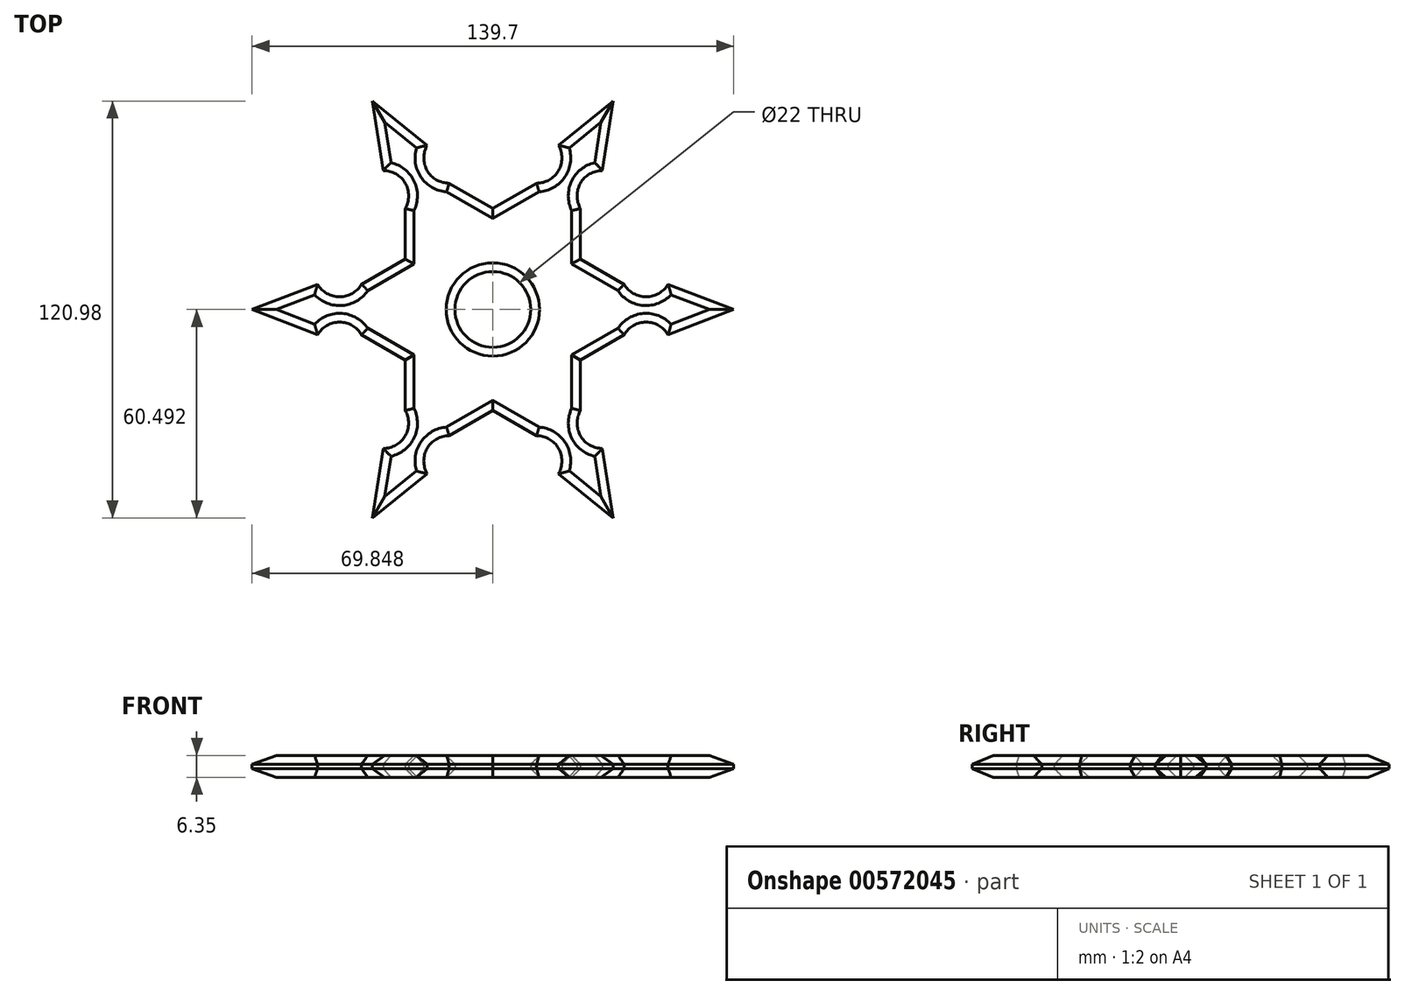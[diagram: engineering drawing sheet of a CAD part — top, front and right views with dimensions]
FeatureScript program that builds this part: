
annotation { "Feature Type Name" : "Feature", "Feature Type Description" : "" }
export const myFeature = defineFeature(function(context is Context, id is Id, definition is map)
    precondition{}
    {
        {
            var Q0;
            Q0=qCreatedBy(makeId("Top.planeOp"),FACE);
            var sketch = newSketch(context, id + "F0", { "sketchPlane" : qUnion([Q0])});
            skCircle(sketch, "E0.cCircle", {"center": v(-16.34, 15.72) * mm, "radius": 25.4 * mm, "construction": true});
            skLineSegment(sketch, "E0.0", {"start": v(9.06, 30.39) * mm, "end": v(9.06, 1.06) * mm});
            skLineSegment(sketch, "E0.1", {"start": v(9.06, 1.06) * mm, "end": v(-16.34, -13.6) * mm});
            skLineSegment(sketch, "E0.2", {"start": v(-16.34, -13.6) * mm, "end": v(-41.74, 1.06) * mm});
            skLineSegment(sketch, "E0.3", {"start": v(-41.74, 1.06) * mm, "end": v(-41.74, 30.39) * mm});
            skLineSegment(sketch, "E0.4", {"start": v(-41.74, 30.39) * mm, "end": v(-16.34, 45.05) * mm});
            skLineSegment(sketch, "E0.5", {"start": v(-16.34, 45.05) * mm, "end": v(9.06, 30.39) * mm});
            skPoint(sketch, "E0.0.midPoint", {"position": v(9.06, 15.72) * mm});
            skLineSegment(sketch, "E1", {"start": v(-16.34, 45.05) * mm, "end": v(-3.64, 52.38) * mm});
            skLineSegment(sketch, "E2", {"start": v(9.06, 30.39) * mm, "end": v(9.06, 45.05) * mm});
            skLineSegment(sketch, "E3", {"start": v(-3.64, 52.38) * mm, "end": v(9.06, 45.05) * mm});
            skLineSegment(sketch, "E4", {"start": v(-41.74, 30.39) * mm, "end": v(-41.74, 45.05) * mm});
            skLineSegment(sketch, "E5", {"start": v(-16.34, 45.05) * mm, "end": v(-29.04, 52.38) * mm});
            skLineSegment(sketch, "E6", {"start": v(-29.04, 52.38) * mm, "end": v(-41.74, 45.05) * mm});
            skLineSegment(sketch, "E7", {"start": v(-41.74, 30.39) * mm, "end": v(-54.44, 23.05) * mm});
            skLineSegment(sketch, "E8", {"start": v(-41.74, 1.06) * mm, "end": v(-54.44, 8.39) * mm});
            skLineSegment(sketch, "E9", {"start": v(-54.44, 23.05) * mm, "end": v(-54.44, 8.39) * mm});
            skLineSegment(sketch, "E10", {"start": v(-41.74, 1.06) * mm, "end": v(-41.74, -13.6) * mm});
            skPoint(sketch, "E11.endSnap0", {"position": v(-29.04, -6.28) * mm});
            skLineSegment(sketch, "E12", {"start": v(-16.34, -13.6) * mm, "end": v(-29.04, -20.94) * mm});
            skLineSegment(sketch, "E13", {"start": v(-41.74, -13.6) * mm, "end": v(-29.04, -20.94) * mm});
            skLineSegment(sketch, "E14", {"start": v(-16.34, -13.6) * mm, "end": v(-3.64, -20.94) * mm});
            skLineSegment(sketch, "E15", {"start": v(9.06, 1.06) * mm, "end": v(9.06, -13.6) * mm});
            skLineSegment(sketch, "E16", {"start": v(-3.64, -20.94) * mm, "end": v(9.06, -13.6) * mm});
            skLineSegment(sketch, "E17", {"start": v(9.06, 30.39) * mm, "end": v(21.76, 23.05) * mm});
            skLineSegment(sketch, "E18", {"start": v(9.06, 1.06) * mm, "end": v(21.76, 8.39) * mm});
            skLineSegment(sketch, "E19", {"start": v(21.76, 23.05) * mm, "end": v(21.76, 8.39) * mm});
            skLineSegment(sketch, "E20", {"start": v(2.7, 63.38) * mm, "end": v(15.4, 56.05) * mm});
            skPoint(sketch, "E21.endSnap0", {"position": v(-35.4, 48.72) * mm});
            skLineSegment(sketch, "E22", {"start": v(-35.4, 63.38) * mm, "end": v(-48.1, 56.05) * mm});
            skLineSegment(sketch, "E23", {"start": v(-67.14, 23.05) * mm, "end": v(-67.14, 8.39) * mm});
            skPoint(sketch, "E24.endSnap0", {"position": v(-35.4, -17.27) * mm});
            skLineSegment(sketch, "E25", {"start": v(-48.1, -24.6) * mm, "end": v(-35.4, -31.94) * mm});
            skPoint(sketch, "E26.endSnap0", {"position": v(2.7, -17.27) * mm});
            skLineSegment(sketch, "E27", {"start": v(2.7, -31.94) * mm, "end": v(15.4, -24.6) * mm});
            skLineSegment(sketch, "E28", {"start": v(34.46, 23.05) * mm, "end": v(34.46, 8.39) * mm});
            skPoint(sketch, "E29.endSnap0", {"position": v(-41.74, 59.72) * mm});
            skPoint(sketch, "E30.endSnap0", {"position": v(-60.8, 8.39) * mm});
            skArc(sketch, "E31", {"start": v(-41.74, 45.05) * mm, "mid": v(-41.74, 52.38) * mm, "end": v(-48.1, 56.05) * mm});
            skArc(sketch, "E32", {"start": v(-35.4, 63.38) * mm, "mid": v(-35.4, 56.05) * mm, "end": v(-29.04, 52.38) * mm});
            skArc(sketch, "E33", {"start": v(-3.64, 52.38) * mm, "mid": v(2.7, 56.05) * mm, "end": v(2.7, 63.38) * mm});
            skArc(sketch, "E34", {"start": v(15.4, 56.05) * mm, "mid": v(9.06, 52.38) * mm, "end": v(9.06, 45.05) * mm});
            skArc(sketch, "E35", {"start": v(-67.14, 23.05) * mm, "mid": v(-60.8, 19.39) * mm, "end": v(-54.44, 23.05) * mm});
            skArc(sketch, "E36", {"start": v(-54.44, 8.39) * mm, "mid": v(-60.8, 12.06) * mm, "end": v(-67.14, 8.39) * mm});
            skArc(sketch, "E37", {"start": v(21.76, 23.05) * mm, "mid": v(28.1, 19.39) * mm, "end": v(34.46, 23.05) * mm});
            skArc(sketch, "E38", {"start": v(34.46, 8.39) * mm, "mid": v(28.1, 12.06) * mm, "end": v(21.76, 8.39) * mm});
            skArc(sketch, "E39", {"start": v(9.06, -13.6) * mm, "mid": v(9.06, -20.94) * mm, "end": v(15.4, -24.6) * mm});
            skArc(sketch, "E40", {"start": v(2.7, -31.94) * mm, "mid": v(2.7, -24.6) * mm, "end": v(-3.64, -20.94) * mm});
            skArc(sketch, "E41", {"start": v(-29.04, -20.94) * mm, "mid": v(-35.4, -24.6) * mm, "end": v(-35.4, -31.94) * mm});
            skArc(sketch, "E42", {"start": v(-48.1, -24.6) * mm, "mid": v(-41.74, -20.94) * mm, "end": v(-41.74, -13.6) * mm});
            skLineSegment(sketch, "E43", {"start": v(-41.74, 59.72) * mm, "end": v(-51.27, 76.21) * mm});
            skLineSegment(sketch, "E44", {"start": v(-67.14, 15.72) * mm, "end": v(-86.2, 15.72) * mm});
            skLineSegment(sketch, "E45", {"start": v(9.06, 59.72) * mm, "end": v(18.58, 76.21) * mm});
            skLineSegment(sketch, "E46", {"start": v(34.46, 15.72) * mm, "end": v(53.5, 15.72) * mm});
            skLineSegment(sketch, "E47", {"start": v(-41.74, -28.27) * mm, "end": v(-51.27, -44.77) * mm});
            skLineSegment(sketch, "E48", {"start": v(9.06, -28.27) * mm, "end": v(18.58, -44.77) * mm});
            skLineSegment(sketch, "E49", {"start": v(-51.27, 76.21) * mm, "end": v(-48.1, 56.05) * mm});
            skLineSegment(sketch, "E50", {"start": v(-51.27, 76.21) * mm, "end": v(-35.4, 63.38) * mm});
            skLineSegment(sketch, "E51", {"start": v(-86.2, 15.72) * mm, "end": v(-67.14, 23.05) * mm});
            skLineSegment(sketch, "E52", {"start": v(-86.2, 15.72) * mm, "end": v(-67.14, 8.39) * mm});
            skLineSegment(sketch, "E53", {"start": v(-48.1, -24.6) * mm, "end": v(-51.27, -44.77) * mm});
            skLineSegment(sketch, "E54", {"start": v(-35.4, -31.94) * mm, "end": v(-51.27, -44.77) * mm});
            skLineSegment(sketch, "E55", {"start": v(2.7, -31.94) * mm, "end": v(18.58, -44.77) * mm});
            skLineSegment(sketch, "E56", {"start": v(15.4, -24.6) * mm, "end": v(18.58, -44.77) * mm});
            skLineSegment(sketch, "E57", {"start": v(34.46, 23.05) * mm, "end": v(53.5, 15.72) * mm});
            skLineSegment(sketch, "E58", {"start": v(53.5, 15.72) * mm, "end": v(34.46, 8.39) * mm});
            skLineSegment(sketch, "E59", {"start": v(2.7, 63.38) * mm, "end": v(18.58, 76.21) * mm});
            skLineSegment(sketch, "E60", {"start": v(15.4, 56.05) * mm, "end": v(18.58, 76.21) * mm});
            skCircle(sketch, "E61", {"center": v(-16.34, 15.72) * mm, "radius": 11 * mm});
            skLineSegment(sketch, "E62", {"start": v(-51.27, 76.21) * mm, "end": v(-86.2, 15.72) * mm});
            skLineSegment(sketch, "E63", {"start": v(-86.2, 15.72) * mm, "end": v(-51.27, -44.77) * mm});
            skLineSegment(sketch, "E64", {"start": v(-51.27, -44.77) * mm, "end": v(18.58, -44.77) * mm});
            skLineSegment(sketch, "E65", {"start": v(18.58, -44.77) * mm, "end": v(53.5, 15.72) * mm});
            skLineSegment(sketch, "E66", {"start": v(53.5, 15.72) * mm, "end": v(18.58, 76.21) * mm});
            skLineSegment(sketch, "E67", {"start": v(18.58, 76.21) * mm, "end": v(-51.27, 76.21) * mm});
            skLineSegment(sketch, "E68", {"start": v(36.05, 45.97) * mm, "end": v(15.4, 26.72) * mm});
            skLineSegment(sketch, "E69", {"start": v(-16.34, 76.21) * mm, "end": v(-22.7, 48.72) * mm});
            skLineSegment(sketch, "E70", {"start": v(-22.7, 48.72) * mm, "end": v(-16.34, 76.21) * mm});
            skLineSegment(sketch, "E71", {"start": v(-10, 48.72) * mm, "end": v(-16.34, 76.21) * mm});
            skLineSegment(sketch, "E72", {"start": v(36.05, 45.97) * mm, "end": v(9.06, 37.72) * mm});
            skLineSegment(sketch, "E73", {"start": v(15.4, 4.72) * mm, "end": v(36.05, -14.52) * mm});
            skLineSegment(sketch, "E74", {"start": v(36.05, -14.52) * mm, "end": v(9.06, -6.28) * mm});
            skLineSegment(sketch, "E75", {"start": v(-22.7, -17.27) * mm, "end": v(-16.34, -44.77) * mm});
            skLineSegment(sketch, "E76", {"start": v(-16.34, -44.77) * mm, "end": v(-10, -17.27) * mm});
            skLineSegment(sketch, "E77", {"start": v(-41.74, 37.72) * mm, "end": v(-68.73, 45.97) * mm});
            skLineSegment(sketch, "E78", {"start": v(-68.73, 45.97) * mm, "end": v(-48.1, 26.72) * mm});
            skLineSegment(sketch, "E79", {"start": v(-48.1, 4.72) * mm, "end": v(-68.73, -14.52) * mm});
            skLineSegment(sketch, "E80", {"start": v(-68.73, -14.52) * mm, "end": v(-41.74, -6.28) * mm});
            skLineSegment(sketch, "E81", {"start": v(-86.2, -44.77) * mm, "end": v(-86.2, 76.21) * mm});
            skLineSegment(sketch, "E82", {"start": v(-86.2, 76.21) * mm, "end": v(53.5, 76.21) * mm});
            skLineSegment(sketch, "E83", {"start": v(53.5, 76.21) * mm, "end": v(53.5, -44.77) * mm});
            skLineSegment(sketch, "E84", {"start": v(53.5, -44.77) * mm, "end": v(-86.2, -44.77) * mm});
            skSolve(sketch);
        }
        {
            var Q0;
            Q0=makeQuery(id+"F0.imprint","IMPRINT",FACE,{"disambiguationData":[TD([[makeQuery(id+"F0.imprint","IMPRINT",EDGE,{"derivedFrom":sQuery(id+"F0.wireOp",EDGE,"E0.4")}),1.0]])]});
            var Q1;
            Q1=makeQuery(id+"F0.imprint","IMPRINT",FACE,{"disambiguationData":[TD([[makeQuery(id+"F0.imprint","IMPRINT",EDGE,{"derivedFrom":sQuery(id+"F0.wireOp",EDGE,"E0.0")}),-1.0]])]});
            var Q2;
            Q2=makeQuery(id+"F0.imprint","IMPRINT",FACE,{"disambiguationData":[TD([[makeQuery(id+"F0.imprint","IMPRINT",EDGE,{"derivedFrom":sQuery(id+"F0.wireOp",EDGE,"E0.3")}),1.0]])]});
            var Q3;
            Q3=makeQuery(id+"F0.imprint","IMPRINT",FACE,{"disambiguationData":[TD([[makeQuery(id+"F0.imprint","IMPRINT",EDGE,{"derivedFrom":sQuery(id+"F0.wireOp",EDGE,"E0.2")}),1.0]])]});
            var Q4;
            Q4=makeQuery(id+"F0.imprint","IMPRINT",FACE,{"disambiguationData":[TD([[makeQuery(id+"F0.imprint","IMPRINT",EDGE,{"derivedFrom":sQuery(id+"F0.wireOp",EDGE,"E0.1")}),1.0]])]});
            var Q5;
            Q5=makeQuery(id+"F0.imprint","IMPRINT",FACE,{"disambiguationData":[TD([[makeQuery(id+"F0.imprint","IMPRINT",EDGE,{"derivedFrom":sQuery(id+"F0.wireOp",EDGE,"E0.0")}),1.0]])]});
            var Q6;
            Q6=makeQuery(id+"F0.imprint","IMPRINT",FACE,{"disambiguationData":[TD([[makeQuery(id+"F0.imprint","IMPRINT",EDGE,{"derivedFrom":sQuery(id+"F0.wireOp",EDGE,"E0.5")}),1.0]])]});
            var Q7;
            {var subQ2=sQuery(id+"F0.wireOp",EDGE,"E43");Q7=makeQuery(id+"F0.imprint","IMPRINT",FACE,{"disambiguationData":[TD([[makeQuery(id+"F0.imprint","IMPRINT",EDGE,{"derivedFrom":subQ2}),-1.0]])]});}
            var Q8;
            {var subQ2=sQuery(id+"F0.wireOp",EDGE,"E43");Q8=makeQuery(id+"F0.imprint","IMPRINT",FACE,{"disambiguationData":[TD([[makeQuery(id+"F0.imprint","IMPRINT",EDGE,{"derivedFrom":subQ2}),1.0]])]});}
            var Q9;
            Q9=makeQuery(id+"F0.imprint","IMPRINT",FACE,{"disambiguationData":[TD([[makeQuery(id+"F0.imprint","IMPRINT",EDGE,{"derivedFrom":sQuery(id+"F0.wireOp",EDGE,"E6")}),-1.0]])]});
            var Q10;
            {var subQ2=sQuery(id+"F0.wireOp",EDGE,"E44");Q10=makeQuery(id+"F0.imprint","IMPRINT",FACE,{"disambiguationData":[TD([[makeQuery(id+"F0.imprint","IMPRINT",EDGE,{"derivedFrom":subQ2}),-1.0]])]});}
            var Q11;
            {var subQ2=sQuery(id+"F0.wireOp",EDGE,"E44");Q11=makeQuery(id+"F0.imprint","IMPRINT",FACE,{"disambiguationData":[TD([[makeQuery(id+"F0.imprint","IMPRINT",EDGE,{"derivedFrom":subQ2}),1.0]])]});}
            var Q12;
            Q12=makeQuery(id+"F0.imprint","IMPRINT",FACE,{"disambiguationData":[TD([[makeQuery(id+"F0.imprint","IMPRINT",EDGE,{"derivedFrom":sQuery(id+"F0.wireOp",EDGE,"E9")}),-1.0]])]});
            var Q13;
            Q13=makeQuery(id+"F0.imprint","IMPRINT",FACE,{"disambiguationData":[TD([[makeQuery(id+"F0.imprint","IMPRINT",EDGE,{"derivedFrom":sQuery(id+"F0.wireOp",EDGE,"E13")}),-1.0]])]});
            var Q14;
            {var subQ2=sQuery(id+"F0.wireOp",EDGE,"E47");Q14=makeQuery(id+"F0.imprint","IMPRINT",FACE,{"disambiguationData":[TD([[makeQuery(id+"F0.imprint","IMPRINT",EDGE,{"derivedFrom":subQ2}),-1.0]])]});}
            var Q15;
            {var subQ2=sQuery(id+"F0.wireOp",EDGE,"E47");Q15=makeQuery(id+"F0.imprint","IMPRINT",FACE,{"disambiguationData":[TD([[makeQuery(id+"F0.imprint","IMPRINT",EDGE,{"derivedFrom":subQ2}),1.0]])]});}
            var Q16;
            {var subQ2=sQuery(id+"F0.wireOp",EDGE,"E48");Q16=makeQuery(id+"F0.imprint","IMPRINT",FACE,{"disambiguationData":[TD([[makeQuery(id+"F0.imprint","IMPRINT",EDGE,{"derivedFrom":subQ2}),1.0]])]});}
            var Q17;
            {var subQ2=sQuery(id+"F0.wireOp",EDGE,"E48");Q17=makeQuery(id+"F0.imprint","IMPRINT",FACE,{"disambiguationData":[TD([[makeQuery(id+"F0.imprint","IMPRINT",EDGE,{"derivedFrom":subQ2}),-1.0]])]});}
            var Q18;
            Q18=makeQuery(id+"F0.imprint","IMPRINT",FACE,{"disambiguationData":[TD([[makeQuery(id+"F0.imprint","IMPRINT",EDGE,{"derivedFrom":sQuery(id+"F0.wireOp",EDGE,"E16")}),-1.0]])]});
            var Q19;
            {var subQ2=sQuery(id+"F0.wireOp",EDGE,"E46");Q19=makeQuery(id+"F0.imprint","IMPRINT",FACE,{"disambiguationData":[TD([[makeQuery(id+"F0.imprint","IMPRINT",EDGE,{"derivedFrom":subQ2}),-1.0]])]});}
            var Q20;
            Q20=makeQuery(id+"F0.imprint","IMPRINT",FACE,{"disambiguationData":[TD([[makeQuery(id+"F0.imprint","IMPRINT",EDGE,{"derivedFrom":sQuery(id+"F0.wireOp",EDGE,"E19")}),1.0]])]});
            var Q21;
            {var subQ2=sQuery(id+"F0.wireOp",EDGE,"E46");Q21=makeQuery(id+"F0.imprint","IMPRINT",FACE,{"disambiguationData":[TD([[makeQuery(id+"F0.imprint","IMPRINT",EDGE,{"derivedFrom":subQ2}),1.0]])]});}
            var Q22;
            Q22=makeQuery(id+"F0.imprint","IMPRINT",FACE,{"disambiguationData":[TD([[makeQuery(id+"F0.imprint","IMPRINT",EDGE,{"derivedFrom":sQuery(id+"F0.wireOp",EDGE,"E3")}),1.0]])]});
            var Q23;
            {var subQ2=sQuery(id+"F0.wireOp",EDGE,"E45");Q23=makeQuery(id+"F0.imprint","IMPRINT",FACE,{"disambiguationData":[TD([[makeQuery(id+"F0.imprint","IMPRINT",EDGE,{"derivedFrom":subQ2}),1.0]])]});}
            var Q24;
            {var subQ2=sQuery(id+"F0.wireOp",EDGE,"E45");Q24=makeQuery(id+"F0.imprint","IMPRINT",FACE,{"disambiguationData":[TD([[makeQuery(id+"F0.imprint","IMPRINT",EDGE,{"derivedFrom":subQ2}),-1.0]])]});}
            extrude(context, id + "F1", {"entities" : qUnion([Q0, Q1, Q2, Q3, Q4, Q5, Q6, Q7, Q8, Q9, Q10, Q11, Q12, Q13, Q14, Q15, Q16, Q17, Q18, Q19, Q20, Q21, Q22, Q23, Q24]), "depth" : 6.35 * mm, "offsetDistance" : 25.4 * mm});
        }
        {
            var Q0;
            Q0=makeQuery(id+"F1.opExtrude","CAP_FACE",FACE,{"disambiguationData":[OSD([sQuery(id+"F0.wireOp",EDGE,"E1"),sQuery(id+"F0.wireOp",EDGE,"E2"),sQuery(id+"F0.wireOp",EDGE,"E4"),sQuery(id+"F0.wireOp",EDGE,"E5"),sQuery(id+"F0.wireOp",EDGE,"E7"),sQuery(id+"F0.wireOp",EDGE,"E8"),sQuery(id+"F0.wireOp",EDGE,"E10"),sQuery(id+"F0.wireOp",EDGE,"E12"),sQuery(id+"F0.wireOp",EDGE,"E14"),sQuery(id+"F0.wireOp",EDGE,"E15"),sQuery(id+"F0.wireOp",EDGE,"E17"),sQuery(id+"F0.wireOp",EDGE,"E18"),sQuery(id+"F0.wireOp",EDGE,"E31"),sQuery(id+"F0.wireOp",EDGE,"E32"),sQuery(id+"F0.wireOp",EDGE,"E33"),sQuery(id+"F0.wireOp",EDGE,"E34"),sQuery(id+"F0.wireOp",EDGE,"E35"),sQuery(id+"F0.wireOp",EDGE,"E36"),sQuery(id+"F0.wireOp",EDGE,"E37"),sQuery(id+"F0.wireOp",EDGE,"E38"),sQuery(id+"F0.wireOp",EDGE,"E39"),sQuery(id+"F0.wireOp",EDGE,"E40"),sQuery(id+"F0.wireOp",EDGE,"E41"),sQuery(id+"F0.wireOp",EDGE,"E42"),sQuery(id+"F0.wireOp",EDGE,"E49"),sQuery(id+"F0.wireOp",EDGE,"E50"),sQuery(id+"F0.wireOp",EDGE,"E51"),sQuery(id+"F0.wireOp",EDGE,"E52"),sQuery(id+"F0.wireOp",EDGE,"E53"),sQuery(id+"F0.wireOp",EDGE,"E54"),sQuery(id+"F0.wireOp",EDGE,"E55"),sQuery(id+"F0.wireOp",EDGE,"E56"),sQuery(id+"F0.wireOp",EDGE,"E57"),sQuery(id+"F0.wireOp",EDGE,"E58"),sQuery(id+"F0.wireOp",EDGE,"E59"),sQuery(id+"F0.wireOp",EDGE,"E60"),sQuery(id+"F0.wireOp",EDGE,"E61")])],"isStart":false});
            var Q1;
            Q1=makeQuery(id+"F1.opExtrude","CAP_FACE",FACE,{"disambiguationData":[OSD([sQuery(id+"F0.wireOp",EDGE,"E1"),sQuery(id+"F0.wireOp",EDGE,"E2"),sQuery(id+"F0.wireOp",EDGE,"E4"),sQuery(id+"F0.wireOp",EDGE,"E5"),sQuery(id+"F0.wireOp",EDGE,"E7"),sQuery(id+"F0.wireOp",EDGE,"E8"),sQuery(id+"F0.wireOp",EDGE,"E10"),sQuery(id+"F0.wireOp",EDGE,"E12"),sQuery(id+"F0.wireOp",EDGE,"E14"),sQuery(id+"F0.wireOp",EDGE,"E15"),sQuery(id+"F0.wireOp",EDGE,"E17"),sQuery(id+"F0.wireOp",EDGE,"E18"),sQuery(id+"F0.wireOp",EDGE,"E31"),sQuery(id+"F0.wireOp",EDGE,"E32"),sQuery(id+"F0.wireOp",EDGE,"E33"),sQuery(id+"F0.wireOp",EDGE,"E34"),sQuery(id+"F0.wireOp",EDGE,"E35"),sQuery(id+"F0.wireOp",EDGE,"E36"),sQuery(id+"F0.wireOp",EDGE,"E37"),sQuery(id+"F0.wireOp",EDGE,"E38"),sQuery(id+"F0.wireOp",EDGE,"E39"),sQuery(id+"F0.wireOp",EDGE,"E40"),sQuery(id+"F0.wireOp",EDGE,"E41"),sQuery(id+"F0.wireOp",EDGE,"E42"),sQuery(id+"F0.wireOp",EDGE,"E49"),sQuery(id+"F0.wireOp",EDGE,"E50"),sQuery(id+"F0.wireOp",EDGE,"E51"),sQuery(id+"F0.wireOp",EDGE,"E52"),sQuery(id+"F0.wireOp",EDGE,"E53"),sQuery(id+"F0.wireOp",EDGE,"E54"),sQuery(id+"F0.wireOp",EDGE,"E55"),sQuery(id+"F0.wireOp",EDGE,"E56"),sQuery(id+"F0.wireOp",EDGE,"E57"),sQuery(id+"F0.wireOp",EDGE,"E58"),sQuery(id+"F0.wireOp",EDGE,"E59"),sQuery(id+"F0.wireOp",EDGE,"E60"),sQuery(id+"F0.wireOp",EDGE,"E61")])],"isStart":true});
            chamfer(context, id + "F2", {"entities" : qUnion([Q0, Q1]), "width" : 2.54 * mm, "tangentPropagation" : true});
        }
    });
